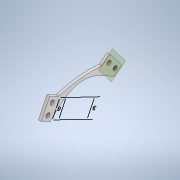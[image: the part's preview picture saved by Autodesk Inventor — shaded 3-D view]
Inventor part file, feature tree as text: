
AUTODESK INVENTOR PART (.ipt)
format: ipt  version: 2020 (Build 240168000, 168)  size: 128,512 bytes
history: native  units: mm
features: other x5, sketch x2, reference x2, plane x1, extrude x1
ambient origin geometry x8: Origin, YZ Plane, XZ Plane, XY Plane, X Axis, Y Axis, Z Axis, Center Point
bodies: Solid1 (feature_tree)
feature tree (11):
  plane  "Work Plane1"
  extrude  "Extrusion1"  [1 undecoded]
  sketch  "Sketch2"
  sketch  "Sketch1"  dims[d0=2.0mm d1=0.0mm]
  reference  "Reference1"
  reference  "Reference2"
  other  "<userpath>\Documents\Inventor\CC_RENEV\belzebub.iam"
  other  "belzebub.iam"
  other  "Part7:1"
  other  "Part7:2"
  other  "Assembly1"
note: 1 required parameter value undecoded (feature->parameter linkage not recoverable at this tier; creation-order binding heuristic only, values carry confidence <= 0.55)
